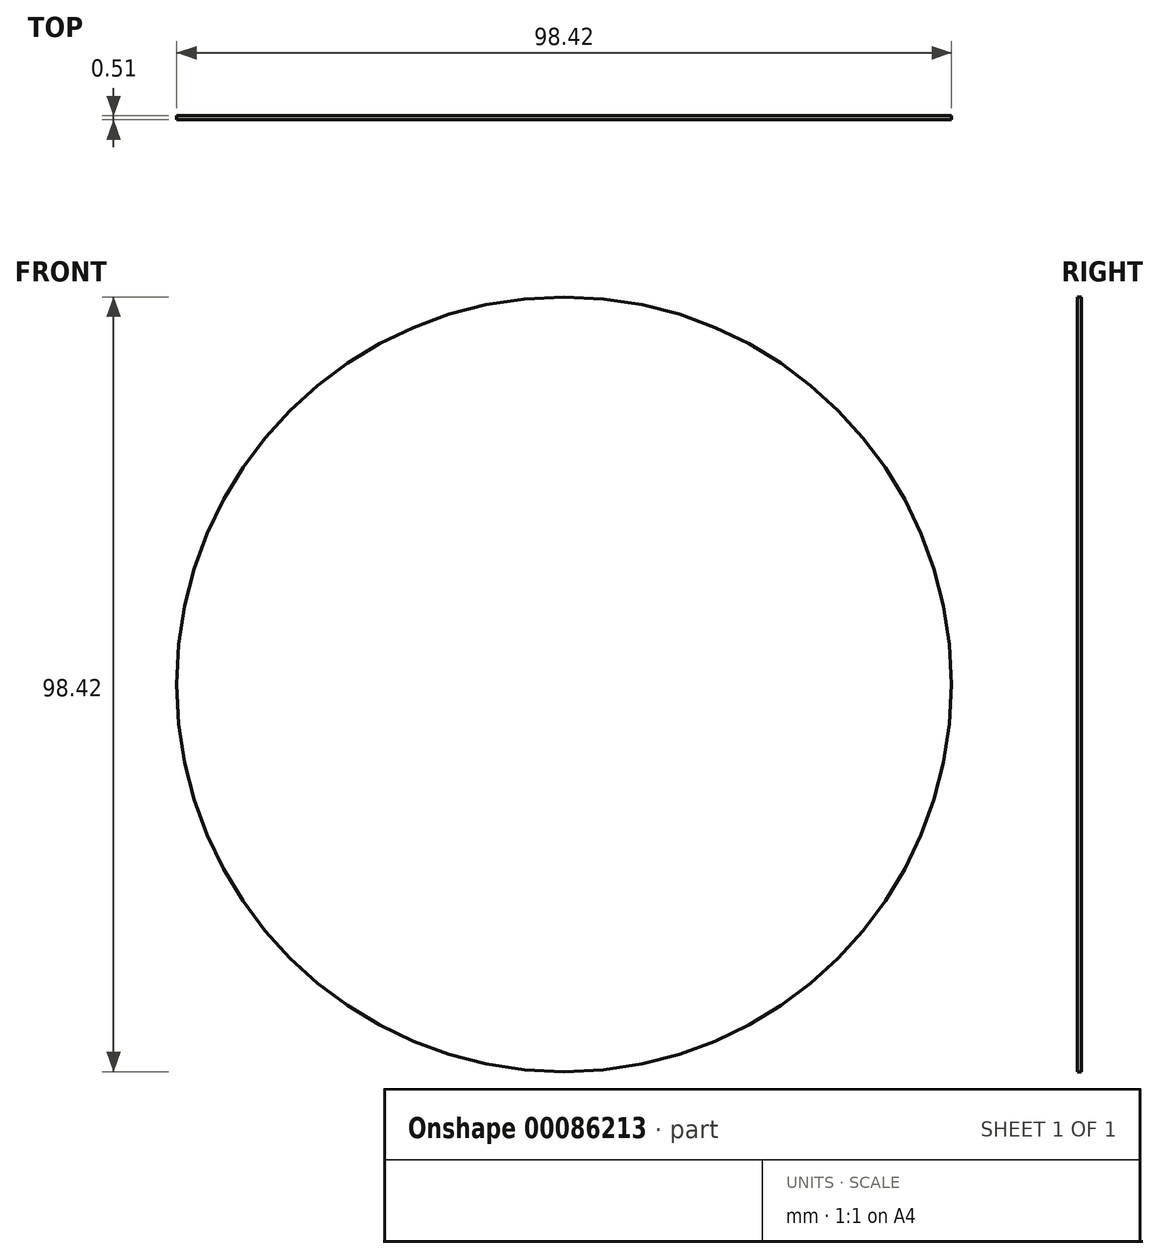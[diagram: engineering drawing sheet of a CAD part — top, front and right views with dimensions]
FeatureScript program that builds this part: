
annotation { "Feature Type Name" : "Feature", "Feature Type Description" : "" }
export const myFeature = defineFeature(function(context is Context, id is Id, definition is map)
    precondition{}
    {
        {
            var Q0;
            Q0=qCreatedBy(makeId("Front.planeOp"),FACE);
            var sketch = newSketch(context, id + "F0", { "sketchPlane" : qUnion([Q0])});
            skCircle(sketch, "E0", {"center": v(0, 0) * mm, "radius": 49.21 * mm});
            skSolve(sketch);
        }
        {
            var Q0;
            Q0 = qSketchRegion(id + "F0", true);
            extrude(context, id + "F1", {"entities" : qUnion([Q0]), "depth" : 0.5 * mm});
        }
    });
